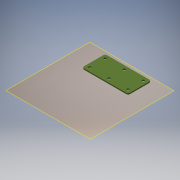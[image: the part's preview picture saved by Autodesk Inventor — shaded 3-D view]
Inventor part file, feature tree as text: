
AUTODESK INVENTOR PART (.ipt)
format: ipt  version: 2016 (Build 200138000, 138)  size: 120,320 bytes
history: native  units: mm
features: reference x6, plane x1, extrude x1, fillet x1, sketch x1
ambient origin geometry x8: Origin, YZ Plane, XZ Plane, XY Plane, X Axis, Y Axis, Z Axis, Center Point
bodies: Solid1 (feature_tree)
feature tree (10):
  plane  "Work Plane1"
  extrude  "Extrusion1"  Depth=3.0mm
  fillet  "Fillet1"  Radius=6.0mm
  sketch  "Sketch2"  dims[d0=6.0mm d1=6.0mm d2=6.0mm d3=6.0mm d4=0.4mm d5=0.4mm d6=0.4mm d7=0.4mm d8=0.4mm d9=0.4mm d10=1.75mm d11=0.0mm d12=3.0mm]
  reference  "Reference1"
  reference  "Reference2"
  reference  "Reference3"
  reference  "Reference4"
  reference  "Reference5"
  reference  "Reference6"
